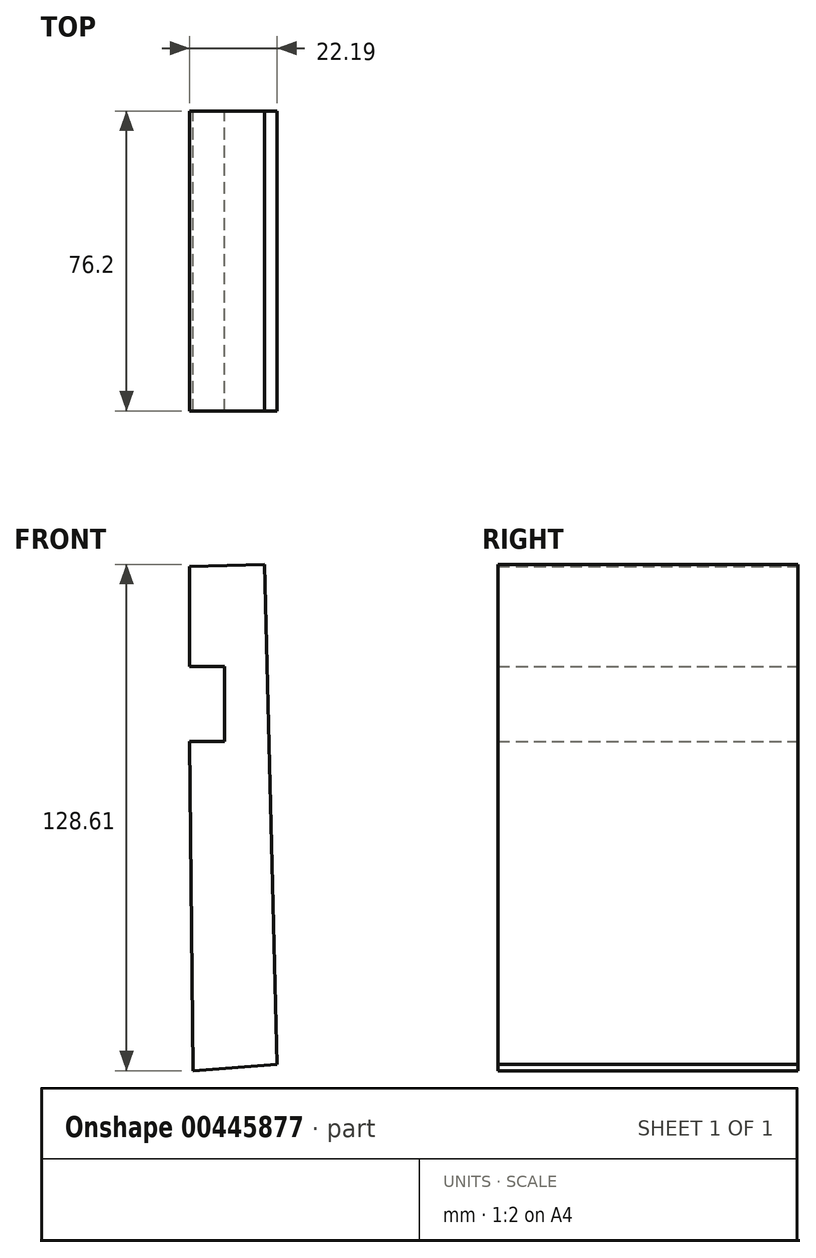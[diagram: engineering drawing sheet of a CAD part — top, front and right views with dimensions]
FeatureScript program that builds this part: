
annotation { "Feature Type Name" : "Feature", "Feature Type Description" : "" }
export const myFeature = defineFeature(function(context is Context, id is Id, definition is map)
    precondition{}
    {
        {
            var Q0;
            Q0=qCreatedBy(makeId("Front.planeOp"),FACE);
            var sketch = newSketch(context, id + "F0", { "sketchPlane" : qUnion([Q0])});
            skLineSegment(sketch, "E0", {"start": v(21.29, -63.89) * mm, "end": v(18.14, 63.07) * mm});
            skLineSegment(sketch, "E1", {"start": v(18.14, 63.07) * mm, "end": v(-0.9, 62.6) * mm});
            skLineSegment(sketch, "E2", {"start": v(-0.9, 62.6) * mm, "end": v(-0.9, 37.2) * mm});
            skLineSegment(sketch, "E3", {"start": v(-0.9, 37.2) * mm, "end": v(7.95, 37.2) * mm});
            skLineSegment(sketch, "E4", {"start": v(7.95, 37.2) * mm, "end": v(7.95, 18.15) * mm});
            skLineSegment(sketch, "E5", {"start": v(7.95, 18.15) * mm, "end": v(-0.9, 18.15) * mm});
            skLineSegment(sketch, "E6", {"start": v(-0.9, 18.15) * mm, "end": v(0, -65.54) * mm});
            skLineSegment(sketch, "E7", {"start": v(0, -65.54) * mm, "end": v(21.29, -63.89) * mm});
            skSolve(sketch);
        }
        {
            var Q0;
            Q0=qSketchRegion(id+"F0",true);
            extrude(context, id + "F1", {"entities" : qUnion([Q0]), "depth" : 76.2 * mm});
        }
    });
